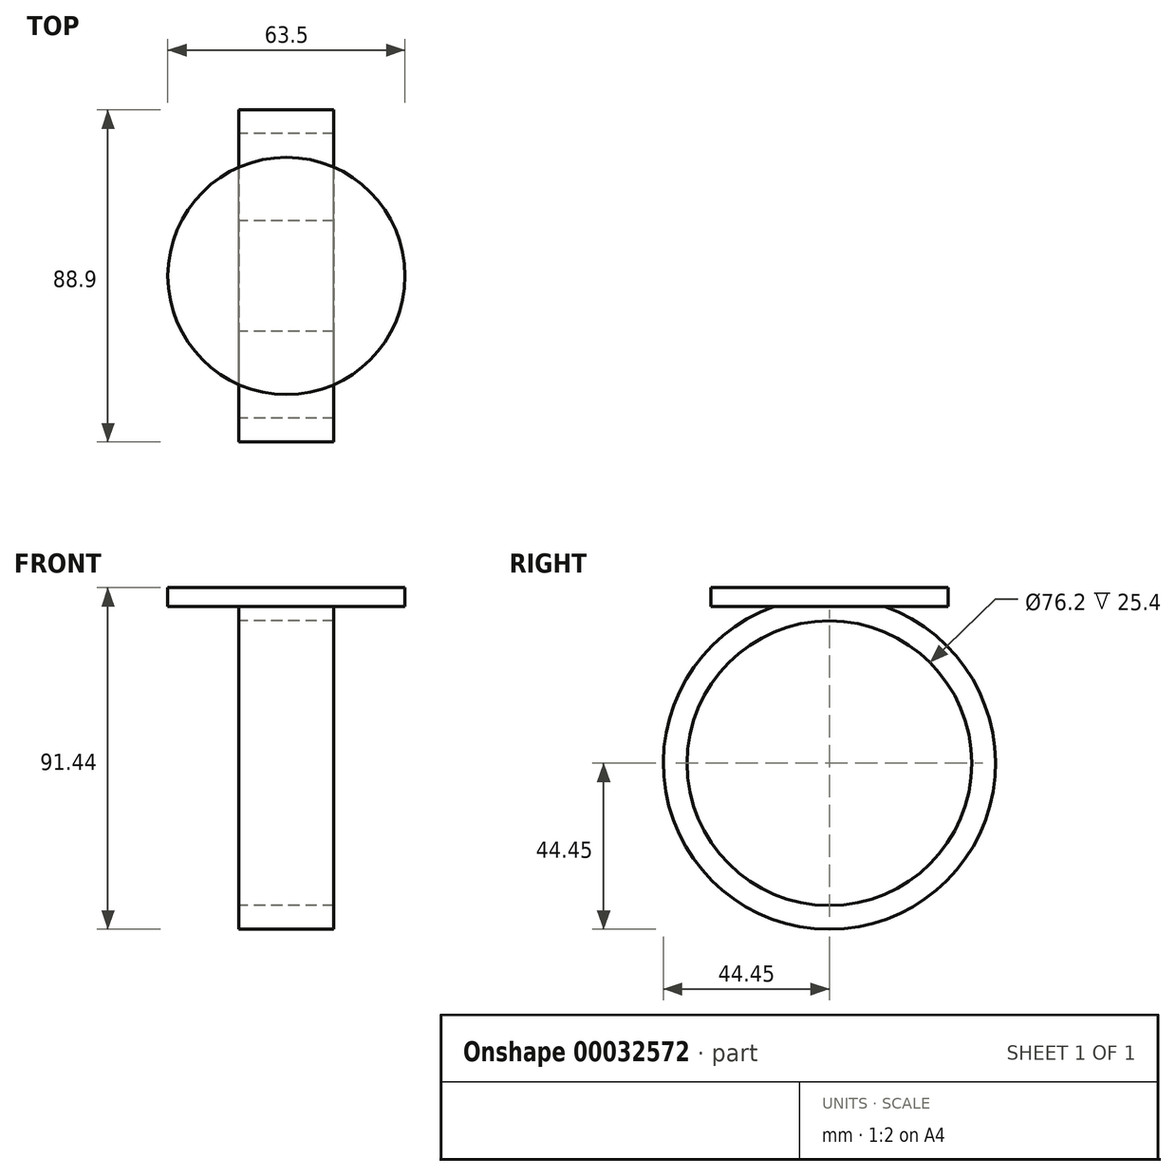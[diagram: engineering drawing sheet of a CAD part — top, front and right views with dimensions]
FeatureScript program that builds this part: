
annotation { "Feature Type Name" : "Feature", "Feature Type Description" : "" }
export const myFeature = defineFeature(function(context is Context, id is Id, definition is map)
    precondition{}
    {
        {
            var Q0;
            Q0=qCreatedBy(makeId("Right.planeOp"),FACE);
            var sketch = newSketch(context, id + "F0", { "sketchPlane" : qUnion([Q0])});
            skCircle(sketch, "E0", {"center": v(0, 0) * mm, "radius": 38.1 * mm});
            skCircle(sketch, "E1", {"center": v(0, 0) * mm, "radius": 44.45 * mm});
            skSolve(sketch);
        }
        {
            var Q0;
            Q0=makeQuery(id+"F0.imprint","IMPRINT",FACE,{"disambiguationData":[TD([[makeQuery(id+"F0.imprint","IMPRINT",EDGE,{"derivedFrom":sQuery(id+"F0.wireOp",EDGE,"E0")}),-1.0]])]});
            extrude(context, id + "F1", {"entities" : qUnion([Q0]), "depth" : 25.4 * mm});
        }
        {
            var Q0;
            Q0=qCreatedBy(makeId("Top.planeOp"),FACE);
            cPlane(context, id + "F2", {"entities" : qUnion([Q0]), "cplaneType" : CPlaneType.OFFSET, "offset" : 44.45 * mm, "width" : 152.4 * mm, "height" : 152.4 * mm});
        }
        {
            var Q0;
            Q0=qCreatedBy(id+"F2.planeOp",FACE);
            var sketch = newSketch(context, id + "F3", { "sketchPlane" : qUnion([Q0])});
            skCircle(sketch, "E2", {"center": v(12.7, 0) * mm, "radius": 31.75 * mm});
            skSolve(sketch);
        }
        {
            var Q0;
            Q0=makeQuery(id+"F3.imprint","IMPRINT",FACE,{"disambiguationData":[TD([[makeQuery(id+"F3.imprint","IMPRINT",EDGE,{"derivedFrom":sQuery(id+"F3.wireOp",EDGE,"E2")}),1.0]])]});
            extrude(context, id + "F4", {"entities" : qUnion([Q0]), "operationType" : NewBodyOperationType.ADD, "endBound" : BoundingType.SYMMETRIC, "depth" : 5.08 * mm});
        }
    });
